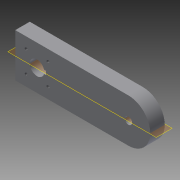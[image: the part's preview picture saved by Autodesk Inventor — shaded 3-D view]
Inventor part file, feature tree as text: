
AUTODESK INVENTOR PART (.ipt)
format: ipt  version: 2016 (Build 200138000, 138)  size: 107,008 bytes
history: native  units: in
note: dims shown in document units (in); Inventor stores cm internally (conversion verified against a paired STEP export)
features: sketch x2, extrude x1, plane x1, hole x1
ambient origin geometry x8: Origin, YZ Plane, XZ Plane, XY Plane, X Axis, Y Axis, Z Axis, Center Point
bodies: Body1 (feature_tree)
feature tree (5):
  extrude  "Extrusion2"  Depth=1.0in
  plane  "Work Plane1"
  hole  "Hole1"  [1 undecoded]
  sketch  "Sketch1"  dims[d0=3.0in d4=1.0in]
  sketch  "Sketch2"  dims[d13=0.5in d14=0.25in d15=6.3in d16=0.13in d17=1.5in d18=1.0in d19=0.0in d20=1.5in d21=1.5in d22=0.75in d23=0.75in d24=0.196in d25=0.75in d26=0.375in d27=0.25in d28=0.5635in d29=1.0in d30=0.8108in]
note: 1 required parameter value undecoded (feature->parameter linkage not recoverable at this tier; creation-order binding heuristic only, values carry confidence <= 0.55)
